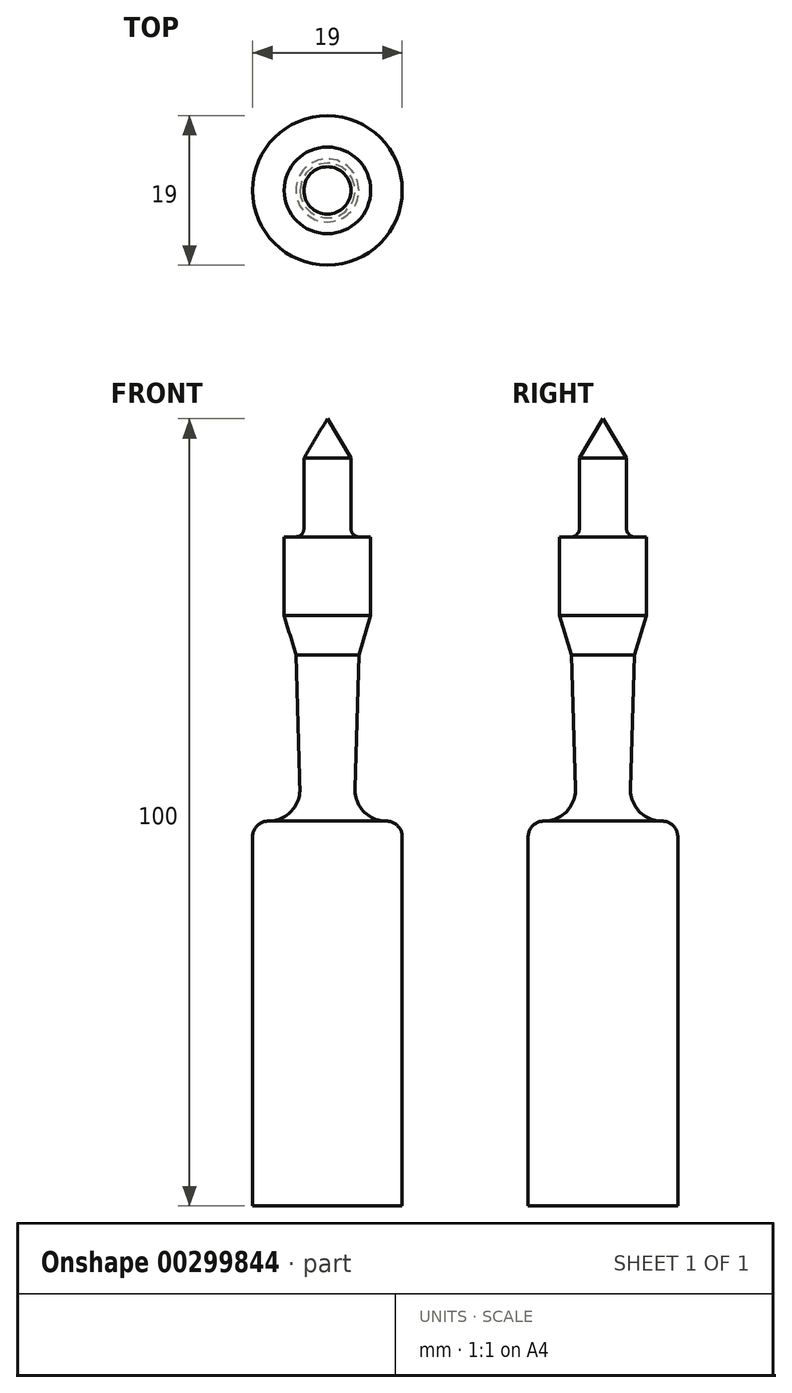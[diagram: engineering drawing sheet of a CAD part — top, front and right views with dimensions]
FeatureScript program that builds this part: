
annotation { "Feature Type Name" : "Feature", "Feature Type Description" : "" }
export const myFeature = defineFeature(function(context is Context, id is Id, definition is map)
    precondition{}
    {
        {
            var Q0;
            Q0=qCreatedBy(makeId("Front.planeOp"),FACE);
            var sketch = newSketch(context, id + "F0", { "sketchPlane" : qUnion([Q0])});
            skLineSegment(sketch, "E0", {"start": v(0, 0) * mm, "end": v(3, -5) * mm});
            skLineSegment(sketch, "E1", {"start": v(3, -5) * mm, "end": v(3, -14) * mm});
            skArc(sketch, "E2", {"start": v(3, -14) * mm, "mid": v(3.3, -14.7) * mm, "end": v(4, -15) * mm});
            skLineSegment(sketch, "E3", {"start": v(4, -15) * mm, "end": v(5.5, -15) * mm});
            skLineSegment(sketch, "E4", {"start": v(5.5, -15) * mm, "end": v(5.5, -25) * mm});
            skLineSegment(sketch, "E5", {"start": v(5.5, -25) * mm, "end": v(4, -30) * mm});
            skArc(sketch, "E6", {"start": v(3.5, -47) * mm, "mid": v(4.63, -49.9) * mm, "end": v(7.5, -51.12) * mm});
            skLineSegment(sketch, "E7", {"start": v(9.5, -100) * mm, "end": v(0, -100) * mm});
            skLineSegment(sketch, "E8", {"start": v(0, -100) * mm, "end": v(0, 0) * mm});
            skLineSegment(sketch, "E9", {"start": v(4, -30) * mm, "end": v(3.5, -47) * mm});
            skArc(sketch, "E10", {"start": v(9.5, -53.12) * mm, "mid": v(8.91, -51.7) * mm, "end": v(7.5, -51.12) * mm});
            skLineSegment(sketch, "E11", {"start": v(9.5, -53.12) * mm, "end": v(9.5, -100) * mm});
            skSolve(sketch);
        }
        {
            var Q0;
            Q0 = qSketchRegion(id + "F0", true);
            var Q1;
            Q1=sQuery(id+"F0.wireOp",EDGE,"E8");
            revolve(context, id + "F1", {"entities" : qUnion([Q0]), "axis" : qUnion([Q1]), "revolveType" : RevolveType.FULL});
        }
    });
